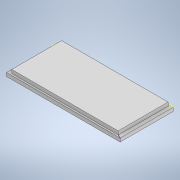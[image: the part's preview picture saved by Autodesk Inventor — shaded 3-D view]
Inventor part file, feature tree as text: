
AUTODESK INVENTOR PART (.ipt)
format: ipt  version: 2020.1 (Build 241239000, 239)  size: 102,400 bytes
history: native  units: mm
features: sketch x3, extrude x2
ambient origin geometry x8: Origin, YZ Plane, XZ Plane, XY Plane, X Axis, Y Axis, Z Axis, Center Point
bodies: Solid1 (feature_tree)
feature tree (5):
  extrude  "Extrusion1"  Depth=15.0mm
  sketch  "Sketch2"  dims[d2=1.0mm d3=0.0mm d4=1.0mm d5=0.0mm]
  extrude  "Extrusion2"  Depth=1.0mm TaperAngle=0.0deg
  sketch  "Sketch1"  dims[d0=32.0mm d1=15.0mm]
  sketch  "Sketch3"
